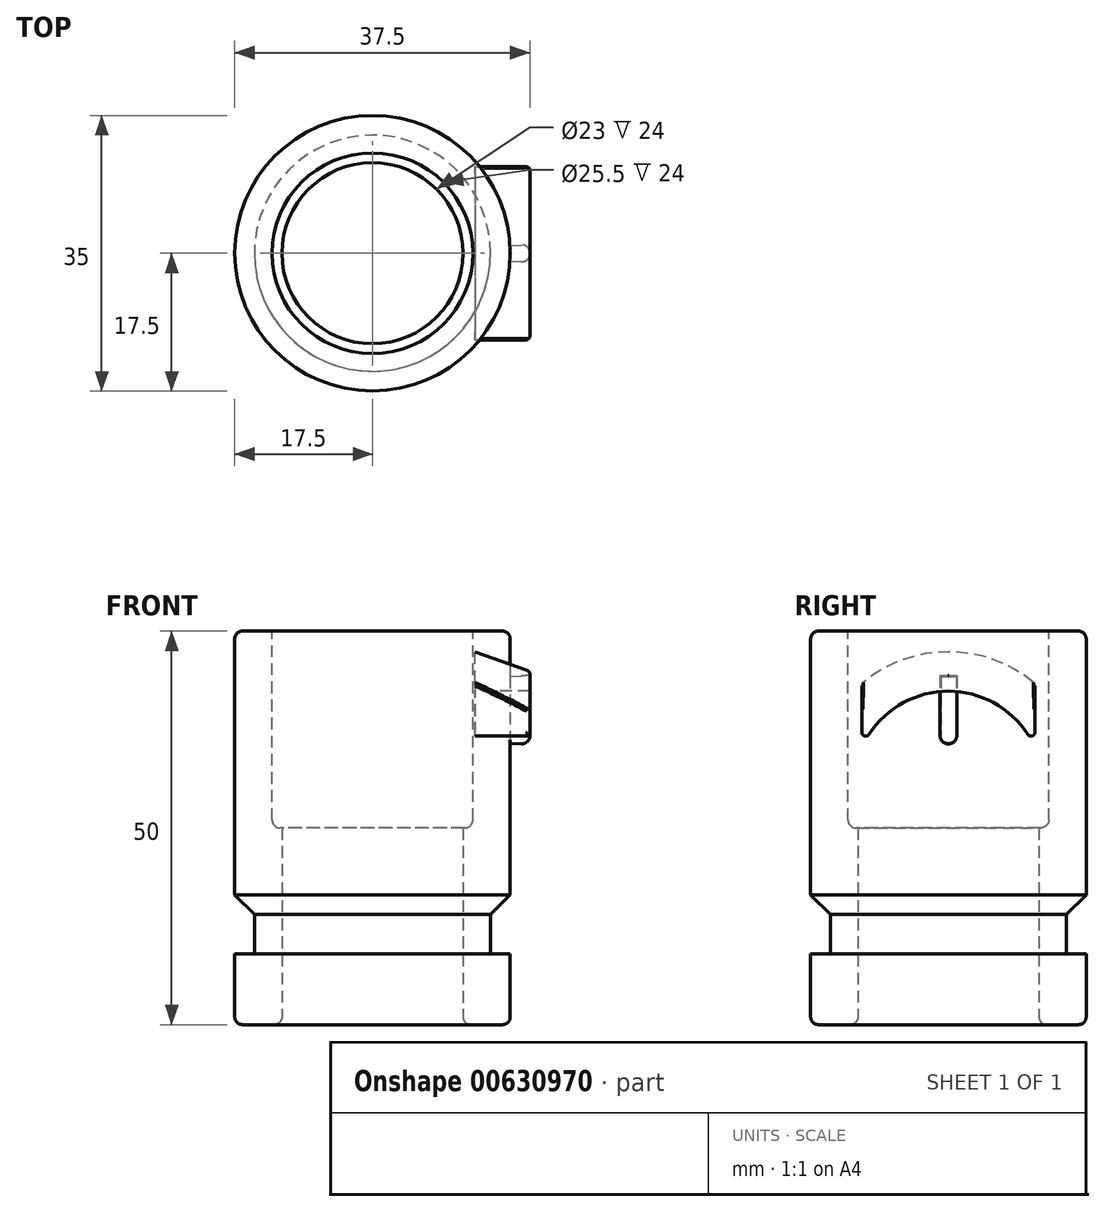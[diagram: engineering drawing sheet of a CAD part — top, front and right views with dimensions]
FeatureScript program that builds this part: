
annotation { "Feature Type Name" : "Feature", "Feature Type Description" : "" }
export const myFeature = defineFeature(function(context is Context, id is Id, definition is map)
    precondition{}
    {
        {
            var Q0;
            Q0=qCreatedBy(makeId("Top.planeOp"),FACE);
            var sketch = newSketch(context, id + "F0", { "sketchPlane" : qUnion([Q0])});
            skCircle(sketch, "E0", {"center": v(0, 0) * mm, "radius": 11.5 * mm});
            skCircle(sketch, "E1", {"center": v(0, 0) * mm, "radius": 17.5 * mm});
            skSolve(sketch);
        }
        {
            var Q0;
            Q0=makeQuery(id+"F0.imprint","IMPRINT",FACE,{"disambiguationData":[TD([[makeQuery(id+"F0.imprint","IMPRINT",EDGE,{"derivedFrom":sQuery(id+"F0.wireOp",EDGE,"E0")}),-1.0]])]});
            extrude(context, id + "F1", {"entities" : qUnion([Q0]), "depth" : 50 * mm, "offsetDistance" : 25 * mm});
        }
        {
            var Q0;
            Q0=qCreatedBy(makeId("Right.planeOp"),FACE);
            var sketch = newSketch(context, id + "F2", { "sketchPlane" : qUnion([Q0])});
            skLineSegment(sketch, "E2", {"start": v(15, 9) * mm, "end": v(15, 14) * mm});
            skLineSegment(sketch, "E3", {"start": v(15, 14) * mm, "end": v(22.81, 21.81) * mm});
            skLineSegment(sketch, "E4", {"start": v(15, 9) * mm, "end": v(22.81, 9) * mm});
            skLineSegment(sketch, "E5", {"start": v(22.81, 9) * mm, "end": v(22.81, 21.81) * mm});
            skLineSegment(sketch, "E6", {"start": v(0, 0) * mm, "end": v(0, -50.29) * mm, "construction": true});
            skSolve(sketch);
        }
        {
            var Q0;
            Q0=makeQuery(id+"F2.imprint","IMPRINT",FACE,{"disambiguationData":[TD([[makeQuery(id+"F2.imprint","IMPRINT",EDGE,{"derivedFrom":sQuery(id+"F2.wireOp",EDGE,"E2")}),-1.0]])]});
            var Q1;
            Q1=sQuery(id+"F2.wireOp",EDGE,"E6");
            var Q2;
            Q2=sQuery(id+"F2.wireOp",EDGE,"E6");
            revolve(context, id + "F3", {"operationType" : NewBodyOperationType.REMOVE, "entities" : qUnion([Q0]), "surfaceEntities" : qUnion([Q1]), "axis" : qUnion([Q2]), "revolveType" : RevolveType.FULL, "oppositeDirection" : true});
        }
        {
            var Q0;
            Q0=makeQuery(id+"F1.opExtrude","CAP_EDGE",EDGE,{"disambiguationData":[OSD([sQuery(id+"F0.wireOp",EDGE,"E1")])],"isStart":true});
            fillet(context, id + "F4", {"entities" : qUnion([Q0]), "radius" : 1 * mm, "allowEdgeOverflow" : false});
        }
        {
            var Q0;
            Q0=makeQuery(id+"F1.opExtrude","CAP_FACE",FACE,{"disambiguationData":[OSD([sQuery(id+"F0.wireOp",EDGE,"E0"),sQuery(id+"F0.wireOp",EDGE,"E1")])],"isStart":false});
            var sketch = newSketch(context, id + "F5", { "sketchPlane" : qUnion([Q0])});
            skCircle(sketch, "E7", {"center": v(0, 0) * mm, "radius": 12.75 * mm});
            skSolve(sketch);
        }
        {
            var Q0;
            Q0=makeQuery(id+"F5.imprint","IMPRINT",FACE,{"disambiguationData":[TD([[makeQuery(id+"F5.imprint","IMPRINT",EDGE,{"derivedFrom":sQuery(id+"F5.wireOp",EDGE,"E7")}),1.0]])]});
            extrude(context, id + "F6", {"entities" : qUnion([Q0]), "operationType" : NewBodyOperationType.REMOVE, "oppositeDirection" : true, "depth" : 25 * mm, "offsetDistance" : 25 * mm});
        }
        {
            var Q0;
            Q0=qCreatedBy(makeId("Right.planeOp"),FACE);
            cPlane(context, id + "F7", {"entities" : qUnion([Q0]), "cplaneType" : CPlaneType.OFFSET, "offset" : 13 * mm, "width" : 150 * mm, "height" : 150 * mm});
        }
        {
            var Q0;
            Q0=qCreatedBy(id+"F7.planeOp",FACE);
            var sketch = newSketch(context, id + "F8", { "sketchPlane" : qUnion([Q0])});
            skLineSegment(sketch, "E8.bottom", {"start": v(-0.75, 44) * mm, "end": v(0.75, 44) * mm});
            skLineSegment(sketch, "E8.top", {"start": v(-0.75, 36) * mm, "end": v(0.75, 36) * mm});
            skLineSegment(sketch, "E8.left", {"start": v(-0.75, 44) * mm, "end": v(-0.75, 36) * mm});
            skLineSegment(sketch, "E8.right", {"start": v(0.75, 44) * mm, "end": v(0.75, 36) * mm});
            skSolve(sketch);
        }
        {
            var Q0;
            Q0=makeQuery(id+"F8.imprint","IMPRINT",FACE,{"disambiguationData":[TD([[makeQuery(id+"F8.imprint","IMPRINT",EDGE,{"derivedFrom":sQuery(id+"F8.wireOp",EDGE,"E8.bottom")}),-1.0]])]});
            var Q1;
            Q1=sQuery(id+"F8.wireOp",EDGE,"E8.bottom");
            var Q2;
            Q2=sQuery(id+"F8.wireOp",EDGE,"E8.right");
            var Q3;
            Q3=sQuery(id+"F8.wireOp",EDGE,"E8.left");
            var Q4;
            Q4=sQuery(id+"F8.wireOp",EDGE,"E8.top");
            extrude(context, id + "F9", {"entities" : qUnion([Q0]), "operationType" : NewBodyOperationType.ADD, "surfaceEntities" : qUnion([Q1, Q2, Q3, Q4]), "depth" : 7 * mm, "offsetDistance" : 25 * mm, "hasDraft" : true, "draftAngle" : 3 * degree});
        }
        {
            var Q0;
            Q0=makeQuery(id+"F9.opExtrude","CAP_EDGE",EDGE,{"disambiguationData":[OSD([sQuery(id+"F8.wireOp",EDGE,"E8.left")])],"isStart":false});
            var Q1;
            Q1=makeQuery(id+"F9.opExtrude","CAP_EDGE",EDGE,{"disambiguationData":[OSD([sQuery(id+"F8.wireOp",EDGE,"E8.top")])],"isStart":false});
            var Q2;
            Q2=makeQuery(id+"F9.opExtrude","CAP_EDGE",EDGE,{"disambiguationData":[OSD([sQuery(id+"F8.wireOp",EDGE,"E8.right")])],"isStart":false});
            var Q3;
            {var subQ0=sQuery(id+"F8.wireOp",EDGE,"E8.left");var subQ1=sQuery(id+"F8.wireOp",EDGE,"E8.top");Q3=makeQuery(id+"F9.boolean.opBoolean","SPLIT",EDGE,{"disambiguationData":[TD([makeQuery(id+"F1.opExtrude","SWEPT_FACE",FACE,{"disambiguationData":[OSD([sQuery(id+"F0.wireOp",EDGE,"E1")])]})])],"derivedFrom":makeQuery(id+"F9.opExtrude","SWEPT_EDGE",EDGE,{"disambiguationData":[OSD([subQ1,subQ0])]})});}
            var Q4;
            Q4=makeQuery(id+"F6.boolean.opBoolean","COPY",EDGE,{"derivedFrom":makeQuery(id+"F6.opExtrude","CAP_EDGE",EDGE,{"disambiguationData":[OSD([sQuery(id+"F5.wireOp",EDGE,"E7")])],"isStart":false})});
            var Q5;
            {var subQ0=sQuery(id+"F8.wireOp",EDGE,"E8.right");var subQ1=sQuery(id+"F8.wireOp",EDGE,"E8.top");Q5=makeQuery(id+"F9.boolean.opBoolean","SPLIT",EDGE,{"disambiguationData":[TD([makeQuery(id+"F1.opExtrude","SWEPT_FACE",FACE,{"disambiguationData":[OSD([sQuery(id+"F0.wireOp",EDGE,"E1")])]})])],"derivedFrom":makeQuery(id+"F9.opExtrude","SWEPT_EDGE",EDGE,{"disambiguationData":[OSD([subQ1,subQ0])]})});}
            fillet(context, id + "F10", {"entities" : qUnion([Q0, Q1, Q2, Q3, Q4, Q5]), "radius" : 1 * mm, "allowEdgeOverflow" : false});
        }
        {
            var Q0;
            Q0=qCreatedBy(id+"F7.planeOp",FACE);
            var sketch = newSketch(context, id + "F11", { "sketchPlane" : qUnion([Q0])});
            skArc(sketch, "E9", {"start": v(11, 35.16) * mm, "mid": v(0, 42.37) * mm, "end": v(-11, 35.16) * mm});
            skArc(sketch, "E10", {"start": v(11, 43.33) * mm, "mid": v(0, 47.37) * mm, "end": v(-11, 43.33) * mm});
            skLineSegment(sketch, "E11", {"start": v(11, 43.33) * mm, "end": v(11, 35.16) * mm});
            skLineSegment(sketch, "E12", {"start": v(-11, 43.33) * mm, "end": v(-11, 35.16) * mm});
            skPoint(sketch, "E13.orphan", {"position": v(-11, 53.7) * mm});
            skPoint(sketch, "E14.orphan", {"position": v(11, 54.5) * mm});
            skSolve(sketch);
        }
        {
            var Q0;
            Q0=makeQuery(id+"F11.imprint","IMPRINT",FACE,{"disambiguationData":[TD([[makeQuery(id+"F11.imprint","IMPRINT",EDGE,{"derivedFrom":sQuery(id+"F11.wireOp",EDGE,"E9")}),-1.0]])]});
            var Q1;
            Q1=makeQuery(id+"F9.opExtrude","CAP_FACE",FACE,{"disambiguationData":[OSD([sQuery(id+"F8.wireOp",EDGE,"E8.bottom"),sQuery(id+"F8.wireOp",EDGE,"E8.top"),sQuery(id+"F8.wireOp",EDGE,"E8.left"),sQuery(id+"F8.wireOp",EDGE,"E8.right")])],"isStart":false});
            extrude(context, id + "F12", {"entities" : qUnion([Q0]), "endBound" : BoundingType.UP_TO_SURFACE, "depth" : 25 * mm, "endBoundEntityFace" : qUnion([Q1]), "offsetDistance" : 25 * mm});
        }
        {
            var Q0;
            Q0=makeQuery(id+"F12.opExtrude","CAP_EDGE",EDGE,{"disambiguationData":[OSD([sQuery(id+"F11.wireOp",EDGE,"E10")])],"isStart":false});
            chamfer(context, id + "F13", {"entities" : qUnion([Q0]), "chamferType" : ChamferType.TWO_OFFSETS, "width1" : 2.5 * mm, "oppositeDirection" : false, "width2" : 7 * mm, "tangentPropagation" : true});
        }
        {
            var Q0;
            Q0=makeQuery(id+"F13.opChamfer","BLEND_EDGE",EDGE,{"blendedFrom":[makeQuery(id+"F12.opExtrude","CAP_EDGE",EDGE,{"disambiguationData":[OSD([sQuery(id+"F11.wireOp",EDGE,"E10")])],"isStart":false}),makeQuery(id+"F12.opExtrude","SWEPT_FACE",FACE,{"disambiguationData":[OSD([sQuery(id+"F11.wireOp",EDGE,"E12")])]})],"blendedInto":[makeQuery(id+"F12.opExtrude","SWEPT_FACE",FACE,{"disambiguationData":[OSD([sQuery(id+"F11.wireOp",EDGE,"E12")])]})]});
            var Q1;
            {var subQ0=sQuery(id+"F11.wireOp",EDGE,"E10");Q1=makeQuery(id+"F13.opChamfer","BLEND_EDGE",EDGE,{"blendedFrom":[makeQuery(id+"F12.opExtrude","CAP_EDGE",EDGE,{"disambiguationData":[OSD([subQ0])],"isStart":false}),makeQuery(id+"F12.opExtrude","CAP_FACE",FACE,{"disambiguationData":[OSD([sQuery(id+"F11.wireOp",EDGE,"E9"),subQ0,sQuery(id+"F11.wireOp",EDGE,"E11"),sQuery(id+"F11.wireOp",EDGE,"E12")])],"isStart":false})],"blendedInto":[makeQuery(id+"F12.opExtrude","CAP_FACE",FACE,{"disambiguationData":[OSD([sQuery(id+"F11.wireOp",EDGE,"E9"),subQ0,sQuery(id+"F11.wireOp",EDGE,"E11"),sQuery(id+"F11.wireOp",EDGE,"E12")])],"isStart":false})]});}
            var Q2;
            Q2=makeQuery(id+"F13.opChamfer","BLEND_EDGE",EDGE,{"blendedFrom":[makeQuery(id+"F12.opExtrude","CAP_EDGE",EDGE,{"disambiguationData":[OSD([sQuery(id+"F11.wireOp",EDGE,"E10")])],"isStart":false}),makeQuery(id+"F12.opExtrude","SWEPT_FACE",FACE,{"disambiguationData":[OSD([sQuery(id+"F11.wireOp",EDGE,"E11")])]})],"blendedInto":[makeQuery(id+"F12.opExtrude","SWEPT_FACE",FACE,{"disambiguationData":[OSD([sQuery(id+"F11.wireOp",EDGE,"E11")])]})]});
            var Q3;
            Q3=makeQuery(id+"F12.opExtrude","CAP_EDGE",EDGE,{"disambiguationData":[OSD([sQuery(id+"F11.wireOp",EDGE,"E11")])],"isStart":false});
            var Q4;
            Q4=makeQuery(id+"F12.opExtrude","CAP_EDGE",EDGE,{"disambiguationData":[OSD([sQuery(id+"F11.wireOp",EDGE,"E12")])],"isStart":false});
            var Q5;
            Q5=makeQuery(id+"F12.opExtrude","SWEPT_EDGE",EDGE,{"disambiguationData":[OSD([sQuery(id+"F11.wireOp",EDGE,"E9"),sQuery(id+"F11.wireOp",EDGE,"E12")])]});
            var Q6;
            Q6=makeQuery(id+"F12.opExtrude","SWEPT_EDGE",EDGE,{"disambiguationData":[OSD([sQuery(id+"F11.wireOp",EDGE,"E9"),sQuery(id+"F11.wireOp",EDGE,"E11")])]});
            fillet(context, id + "F14", {"entities" : qUnion([Q0, Q1, Q2, Q3, Q4, Q5, Q6]), "radius" : 0.5 * mm, "tangentPropagation" : true, "allowEdgeOverflow" : false});
        }
        {
            var Q0;
            Q0=makeQuery(id+"F1.opExtrude","CAP_EDGE",EDGE,{"disambiguationData":[OSD([sQuery(id+"F0.wireOp",EDGE,"E1")])],"isStart":false});
            var Q1;
            Q1=makeQuery(id+"F6.boolean.opBoolean","COPY",EDGE,{"derivedFrom":makeQuery(id+"F6.opExtrude","CAP_EDGE",EDGE,{"disambiguationData":[OSD([sQuery(id+"F5.wireOp",EDGE,"E7")])],"isStart":true})});
            fillet(context, id + "F15", {"entities" : qUnion([Q0, Q1]), "radius" : 1 * mm, "tangentPropagation" : true, "allowEdgeOverflow" : false});
        }
        {
            var Q0;
            Q0=makeQuery(id+"F1.opExtrude","CAP_EDGE",EDGE,{"disambiguationData":[OSD([sQuery(id+"F0.wireOp",EDGE,"E0")])],"isStart":true});
            fillet(context, id + "F16", {"entities" : qUnion([Q0]), "radius" : 1 * mm, "tangentPropagation" : true, "allowEdgeOverflow" : false});
        }
    });
